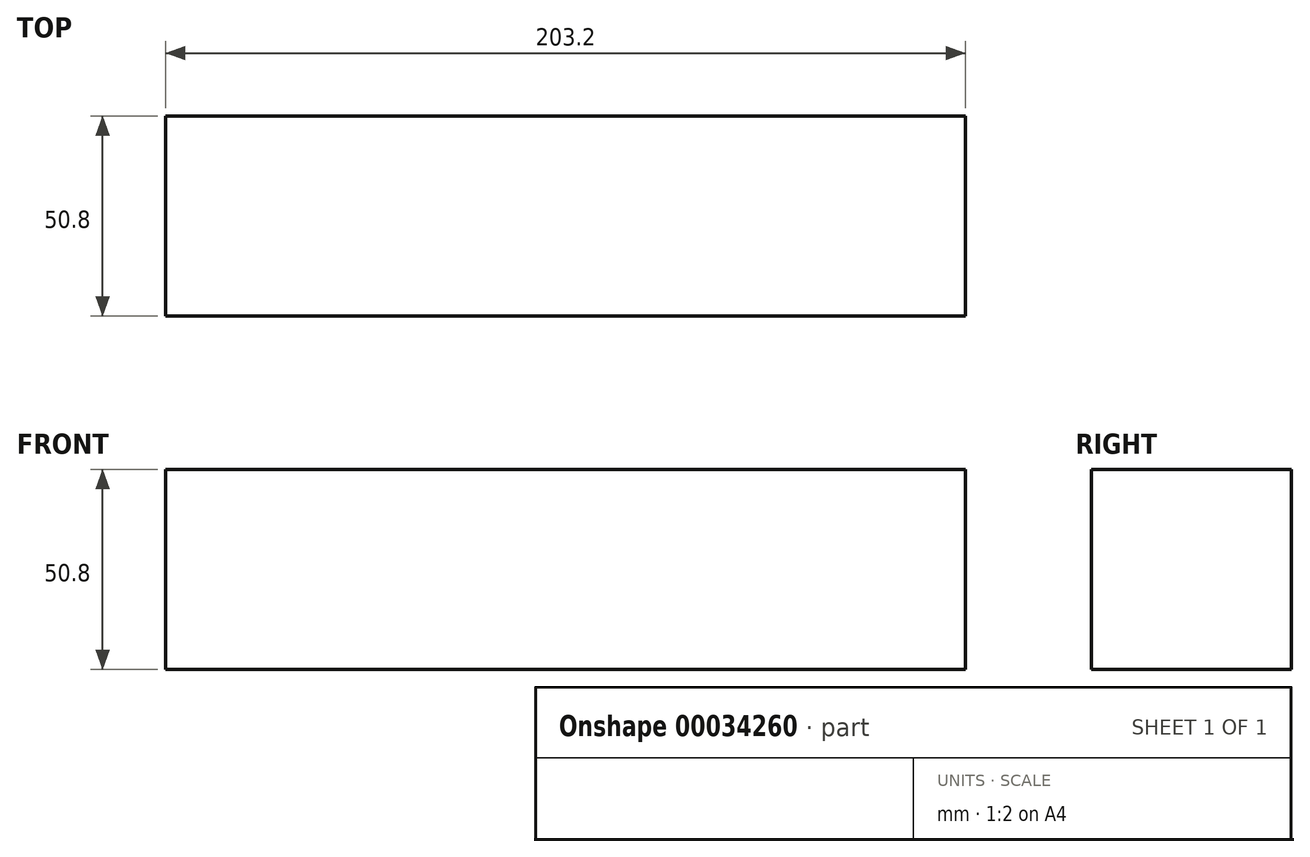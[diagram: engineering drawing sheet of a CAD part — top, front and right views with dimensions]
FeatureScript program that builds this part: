
annotation { "Feature Type Name" : "Feature", "Feature Type Description" : "" }
export const myFeature = defineFeature(function(context is Context, id is Id, definition is map)
    precondition{}
    {
        {
            var Q0;
            Q0=qCreatedBy(makeId("Right.planeOp"),FACE);
            var sketch = newSketch(context, id + "F0", { "sketchPlane" : qUnion([Q0])});
            skLineSegment(sketch, "E0.bottom", {"start": v(0, 0) * mm, "end": v(-50.8, 0) * mm});
            skLineSegment(sketch, "E0.top", {"start": v(0, 50.8) * mm, "end": v(-50.8, 50.8) * mm});
            skLineSegment(sketch, "E0.left", {"start": v(0, 0) * mm, "end": v(0, 50.8) * mm});
            skLineSegment(sketch, "E0.right", {"start": v(-50.8, 0) * mm, "end": v(-50.8, 50.8) * mm});
            skSolve(sketch);
        }
        {
            var Q0;
            Q0=makeQuery(id+"F0.imprint","IMPRINT",FACE,{"disambiguationData":[TD([[makeQuery(id+"F0.imprint","IMPRINT",EDGE,{"derivedFrom":sQuery(id+"F0.wireOp",EDGE,"E0.bottom")}),-1.0]])]});
            extrude(context, id + "F1", {"entities" : qUnion([Q0]), "depth" : 203.2 * mm});
        }
    });
